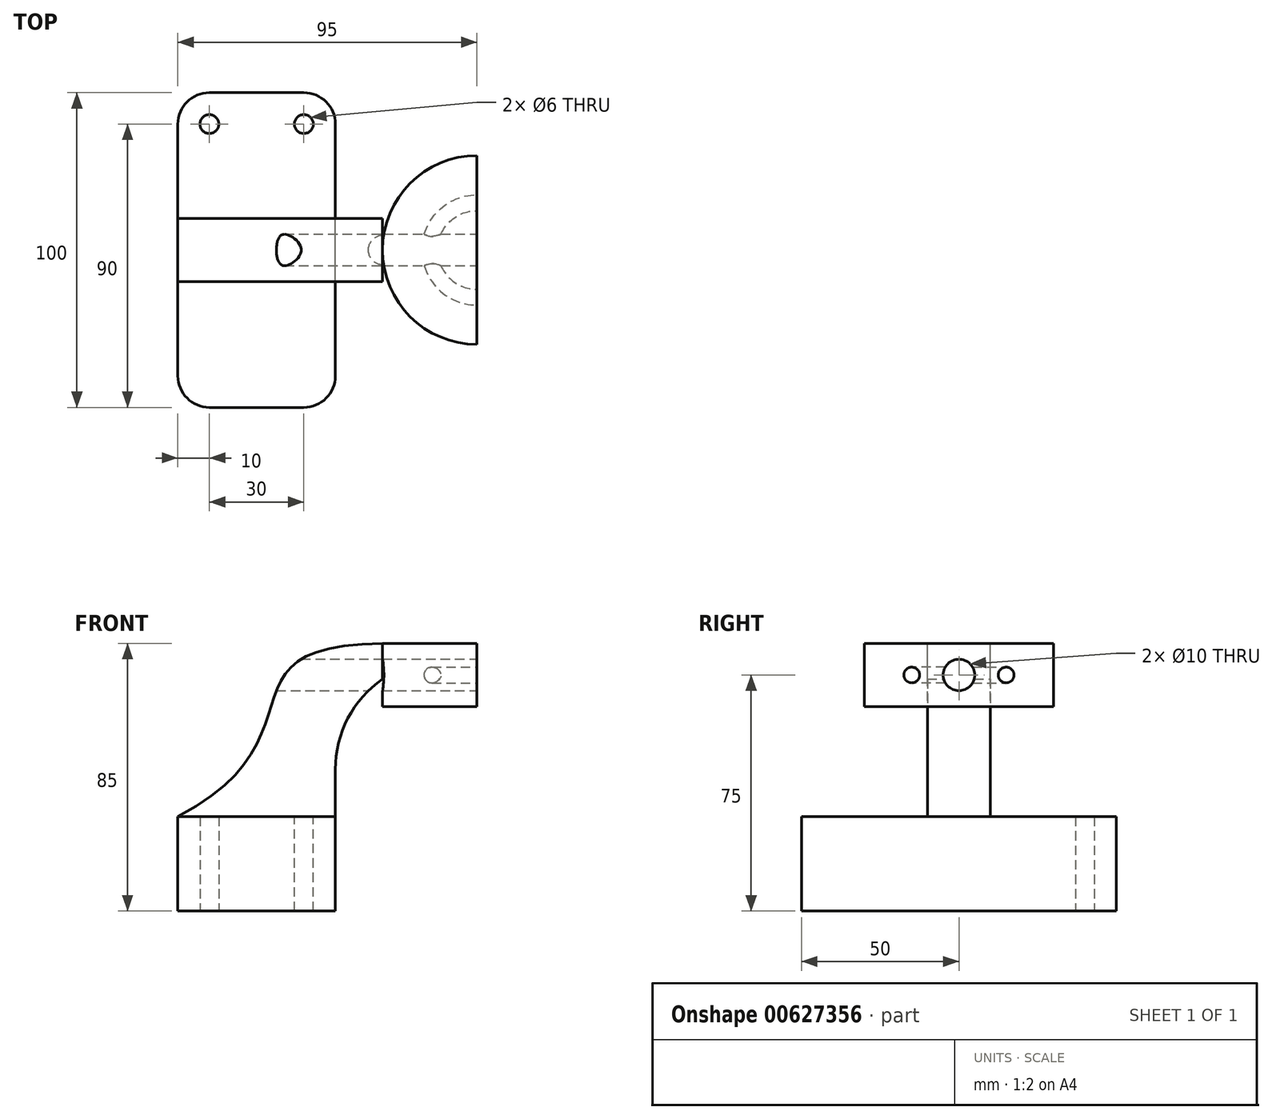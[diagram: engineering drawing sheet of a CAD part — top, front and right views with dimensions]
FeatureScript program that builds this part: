
annotation { "Feature Type Name" : "Feature", "Feature Type Description" : "" }
export const myFeature = defineFeature(function(context is Context, id is Id, definition is map)
    precondition{}
    {
        {
            var Q0;
            Q0=qCreatedBy(makeId("Front.planeOp"),FACE);
            var sketch = newSketch(context, id + "F0", { "sketchPlane" : qUnion([Q0])});
            skLineSegment(sketch, "E0.bottom", {"start": v(25, 15) * mm, "end": v(-25, 15) * mm});
            skLineSegment(sketch, "E0.top", {"start": v(25, -15) * mm, "end": v(-25, -15) * mm});
            skLineSegment(sketch, "E0.left", {"start": v(25, 15) * mm, "end": v(25, -15) * mm});
            skLineSegment(sketch, "E0.right", {"start": v(-25, 15) * mm, "end": v(-25, -15) * mm});
            skPoint(sketch, "E0.middle", {"position": v(0, 0) * mm});
            skLineSegment(sketch, "E1.bottom", {"start": v(70, 50) * mm, "end": v(40, 50) * mm});
            skLineSegment(sketch, "E1.top", {"start": v(70, 70) * mm, "end": v(40, 70) * mm});
            skLineSegment(sketch, "E1.left", {"start": v(70, 50) * mm, "end": v(70, 70) * mm});
            skLineSegment(sketch, "E1.right", {"start": v(40, 50) * mm, "end": v(40, 70) * mm});
            skPoint(sketch, "E1.middle", {"position": v(55, 60) * mm});
            skLineSegment(sketch, "E2", {"start": v(25, 15) * mm, "end": v(25, 30) * mm});
            skArc(sketch, "E3", {"start": v(25, 30) * mm, "mid": v(29.54, 47.23) * mm, "end": v(41.97, 60) * mm});
            skLineSegment(sketch, "E4", {"start": v(41.97, 60) * mm, "end": v(55, 60) * mm});
            skFitSpline(sketch, "E5", {"points": [v(-25, 15) * mm, v(40, 70) * mm], "startDerivative": vector(143.36, 74.81) * mm, "endDerivative": vector(162.72, 1.6) * mm});
            skCircle(sketch, "E6", {"center": v(55, 60) * mm, "radius": 2.5 * mm});
            skSolve(sketch);
        }
        {
            var Q0;
            Q0=makeQuery(id+"F0.imprint","IMPRINT",FACE,{"disambiguationData":[TD([[makeQuery(id+"F0.imprint","IMPRINT",EDGE,{"derivedFrom":sQuery(id+"F0.wireOp",EDGE,"E0.bottom")}),1.0]])]});
            extrude(context, id + "F1", {"entities" : qUnion([Q0]), "endBound" : BoundingType.SYMMETRIC, "depth" : 100 * mm, "offsetDistance" : 25 * mm});
        }
        {
            var Q0;
            Q0=makeQuery(id+"F0.imprint","IMPRINT",FACE,{"disambiguationData":[TD([[makeQuery(id+"F0.imprint","IMPRINT",EDGE,{"derivedFrom":sQuery(id+"F0.wireOp",EDGE,"E0.bottom")}),-1.0]])]});
            extrude(context, id + "F2", {"entities" : qUnion([Q0]), "endBound" : BoundingType.SYMMETRIC, "depth" : 20 * mm, "offsetDistance" : 25 * mm});
        }
        {
            var Q0;
            {var subQ1=sQuery(id+"F0.wireOp",EDGE,"E1.bottom");Q0=makeQuery(id+"F0.imprint","IMPRINT",FACE,{"disambiguationData":[TD([[makeQuery(id+"F0.imprint","IMPRINT",EDGE,{"derivedFrom":subQ1}),-1.0]])]});}
            var Q1;
            Q1=sQuery(id+"F0.wireOp",EDGE,"E1.left");
            revolve(context, id + "F3", {"entities" : qUnion([Q0]), "axis" : qUnion([Q1]), "revolveType" : RevolveType.SYMMETRIC, "angle" : 180 * degree});
        }
        {
            var Q0;
            Q0=makeQuery(id+"F1.opExtrude","CAP_EDGE",EDGE,{"disambiguationData":[OSD([sQuery(id+"F0.wireOp",EDGE,"E0.right")])],"isStart":false});
            var Q1;
            Q1=makeQuery(id+"F1.opExtrude","CAP_EDGE",EDGE,{"disambiguationData":[OSD([sQuery(id+"F0.wireOp",EDGE,"E0.left")])],"isStart":false});
            var Q2;
            Q2=makeQuery(id+"F1.opExtrude","CAP_EDGE",EDGE,{"disambiguationData":[OSD([sQuery(id+"F0.wireOp",EDGE,"E0.left")])],"isStart":true});
            var Q3;
            Q3=makeQuery(id+"F1.opExtrude","CAP_EDGE",EDGE,{"disambiguationData":[OSD([sQuery(id+"F0.wireOp",EDGE,"E0.right")])],"isStart":true});
            fillet(context, id + "F4", {"entities" : qUnion([Q0, Q1, Q2, Q3]), "radius" : 10 * mm, "tangentPropagation" : true, "allowEdgeOverflow" : false});
        }
        {
            var Q0;
            Q0=qCreatedBy(makeId("Top.planeOp"),FACE);
            var sketch = newSketch(context, id + "F5", { "sketchPlane" : qUnion([Q0])});
            skCircle(sketch, "E7", {"center": v(-15, 40) * mm, "radius": 3 * mm});
            skCircle(sketch, "E8", {"center": v(15, 40) * mm, "radius": 3 * mm});
            skSolve(sketch);
        }
        {
            var Q0;
            Q0=makeQuery(id+"F5.imprint","IMPRINT",FACE,{"disambiguationData":[TD([[makeQuery(id+"F5.imprint","IMPRINT",EDGE,{"derivedFrom":sQuery(id+"F5.wireOp",EDGE,"E7")}),1.0]])]});
            extrude(context, id + "F6", {"entities" : qUnion([Q0]), "operationType" : NewBodyOperationType.REMOVE, "endBound" : BoundingType.SYMMETRIC, "depth" : 35 * mm, "offsetDistance" : 25 * mm});
        }
        {
            var Q0;
            Q0=makeQuery(id+"F5.imprint","IMPRINT",FACE,{"disambiguationData":[TD([[makeQuery(id+"F5.imprint","IMPRINT",EDGE,{"derivedFrom":sQuery(id+"F5.wireOp",EDGE,"E8")}),1.0]])]});
            extrude(context, id + "F7", {"entities" : qUnion([Q0]), "operationType" : NewBodyOperationType.REMOVE, "endBound" : BoundingType.SYMMETRIC, "oppositeDirection" : true, "depth" : 30 * mm, "offsetDistance" : 25 * mm});
        }
        {
            var Q0;
            Q0=qCreatedBy(makeId("Right.planeOp"),FACE);
            var sketch = newSketch(context, id + "F8", { "sketchPlane" : qUnion([Q0])});
            skCircle(sketch, "E9", {"center": v(0, 60) * mm, "radius": 5 * mm});
            skSolve(sketch);
        }
        {
            var Q0;
            Q0=makeQuery(id+"F8.imprint","IMPRINT",FACE,{"disambiguationData":[TD([[makeQuery(id+"F8.imprint","IMPRINT",EDGE,{"derivedFrom":sQuery(id+"F8.wireOp",EDGE,"E9")}),1.0]])]});
            extrude(context, id + "F9", {"entities" : qUnion([Q0]), "operationType" : NewBodyOperationType.REMOVE, "endBound" : BoundingType.SYMMETRIC, "oppositeDirection" : true, "depth" : 200 * mm, "offsetDistance" : 25 * mm});
        }
    });
